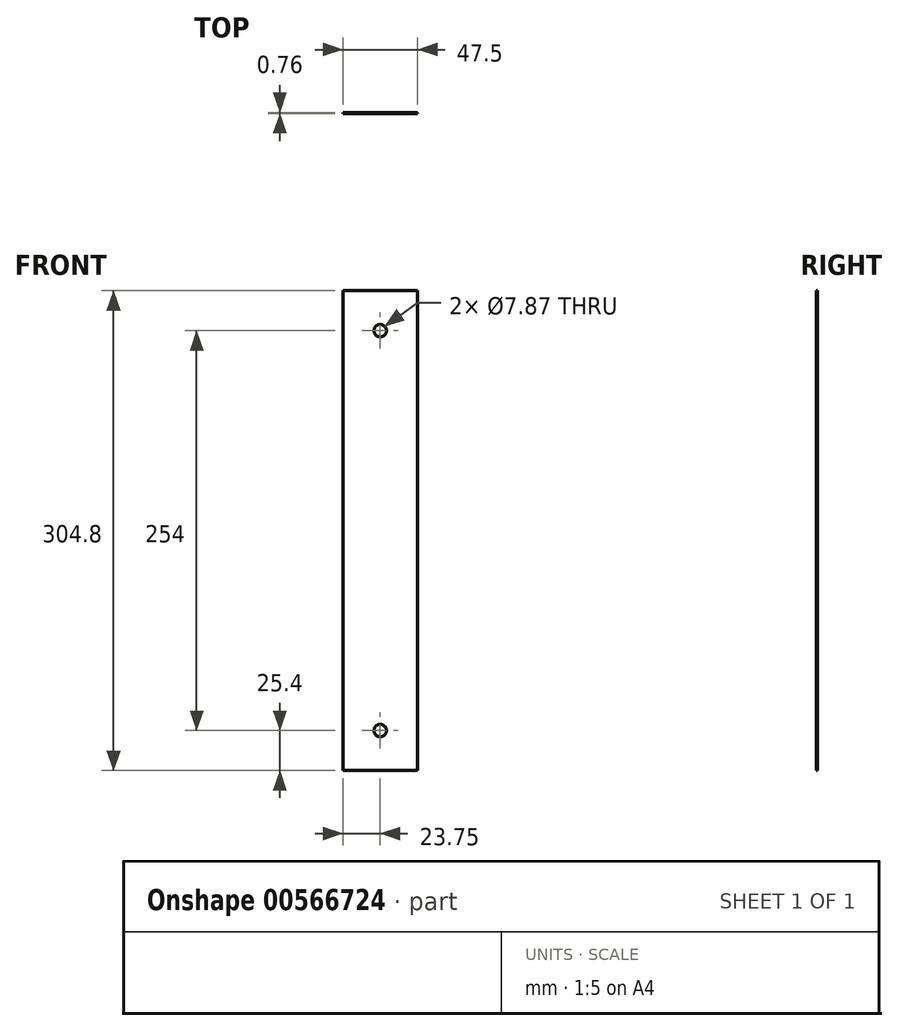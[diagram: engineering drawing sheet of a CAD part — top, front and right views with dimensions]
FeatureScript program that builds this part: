
annotation { "Feature Type Name" : "Feature", "Feature Type Description" : "" }
export const myFeature = defineFeature(function(context is Context, id is Id, definition is map)
    precondition{}
    {
        {
            var Q0;
            Q0=qCreatedBy(makeId("Front.planeOp"),FACE);
            var sketch = newSketch(context, id + "F0", { "sketchPlane" : qUnion([Q0])});
            skLineSegment(sketch, "E0.bottom", {"start": v(23.75, -152.4) * mm, "end": v(-23.75, -152.4) * mm});
            skLineSegment(sketch, "E0.top", {"start": v(23.75, 152.4) * mm, "end": v(-23.75, 152.4) * mm});
            skLineSegment(sketch, "E0.left", {"start": v(23.75, -152.4) * mm, "end": v(23.75, 152.4) * mm});
            skLineSegment(sketch, "E0.right", {"start": v(-23.75, -152.4) * mm, "end": v(-23.75, 152.4) * mm});
            skPoint(sketch, "E0.middle", {"position": v(0, 0) * mm});
            skSolve(sketch);
        }
        {
            var Q0;
            Q0 = qSketchRegion(id + "F0", true);
            extrude(context, id + "F1", {"entities" : qUnion([Q0]), "depth" : 0.76 * mm, "offsetDistance" : 25.4 * mm});
        }
        {
            var Q0;
            Q0=qCreatedBy(makeId("Front.planeOp"),FACE);
            var sketch = newSketch(context, id + "F2", { "sketchPlane" : qUnion([Q0])});
            skPoint(sketch, "E1", {"position": v(0, 127) * mm});
            skCircle(sketch, "E2", {"center": v(0, 127) * mm, "radius": 3.94 * mm});
            skPoint(sketch, "E3", {"position": v(0, -127) * mm});
            skCircle(sketch, "E4", {"center": v(0, -127) * mm, "radius": 3.94 * mm});
            skSolve(sketch);
        }
        {
            var Q0;
            Q0 = qSketchRegion(id + "F2", true);
            extrude(context, id + "F3", {"entities" : qUnion([Q0]), "operationType" : NewBodyOperationType.REMOVE, "endBound" : BoundingType.SYMMETRIC, "depth" : 25.4 * mm, "offsetDistance" : 25.4 * mm});
        }
    });
